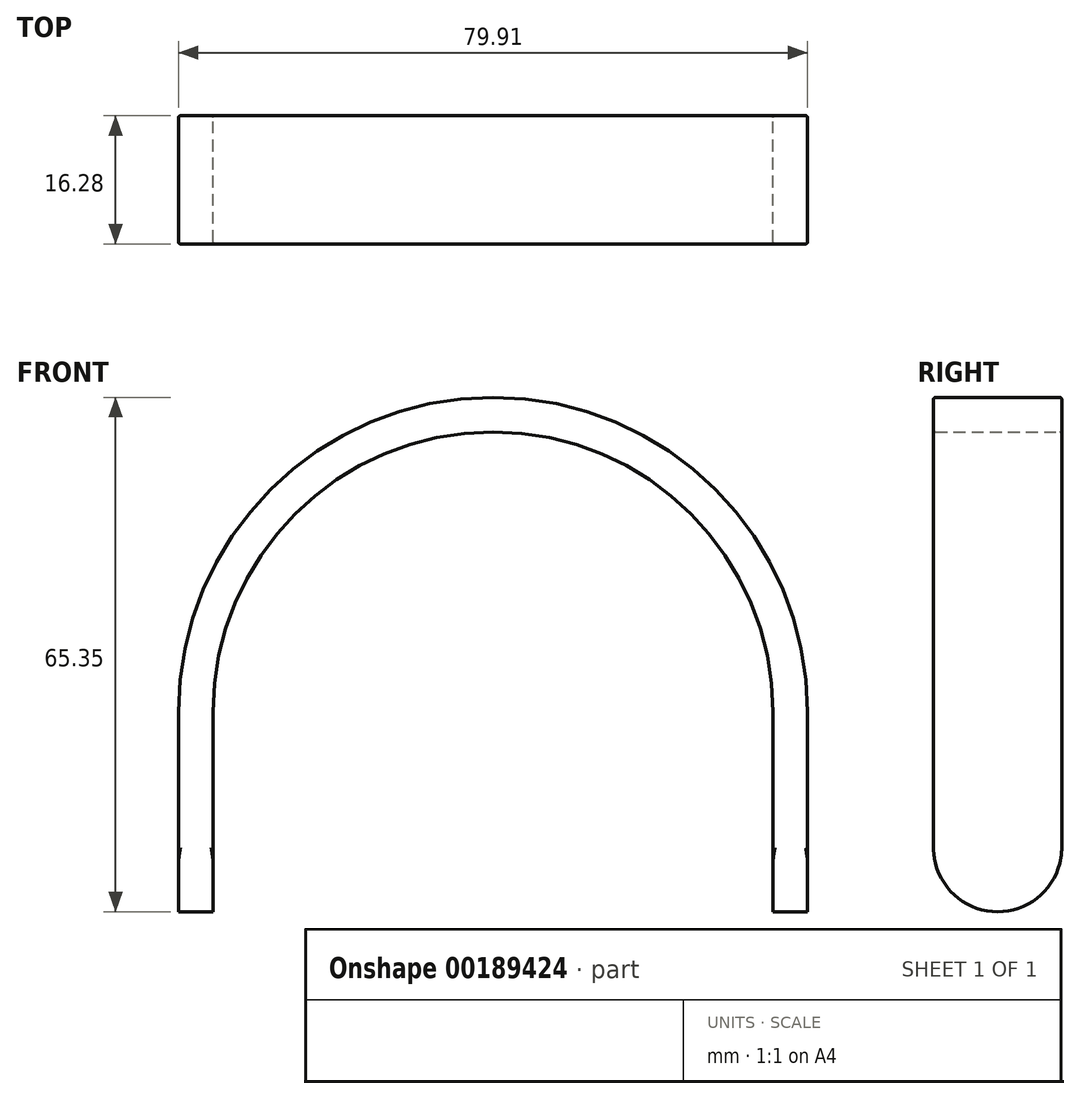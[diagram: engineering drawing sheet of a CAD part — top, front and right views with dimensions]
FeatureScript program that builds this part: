
annotation { "Feature Type Name" : "Feature", "Feature Type Description" : "" }
export const myFeature = defineFeature(function(context is Context, id is Id, definition is map)
    precondition{}
    {
        {
            var Q0;
            Q0=qCreatedBy(makeId("Front.planeOp"),FACE);
            var sketch = newSketch(context, id + "F0", { "sketchPlane" : qUnion([Q0])});
            skArc(sketch, "E0", {"start": v(79.9, 0) * mm, "mid": v(39.95, 39.95) * mm, "end": v(0, 0) * mm});
            skArc(sketch, "E1", {"start": v(75.51, 0) * mm, "mid": v(39.95, 35.56) * mm, "end": v(4.4, 0) * mm});
            skLineSegment(sketch, "E2", {"start": v(4.4, 0) * mm, "end": v(0, 0) * mm});
            skLineSegment(sketch, "E3", {"start": v(75.51, 0) * mm, "end": v(79.9, 0) * mm});
            skSolve(sketch);
        }
        {
            var Q0;
            Q0 = qSketchRegion(id + "F0", true);
            extrude(context, id + "F1", {"entities" : qUnion([Q0]), "depth" : 16.28 * mm});
        }
        {
            var Q0;
            Q0=makeQuery(id+"F1.opExtrude","CAP_EDGE",EDGE,{"disambiguationData":[OSD([sQuery(id+"F0.wireOp",EDGE,"E0")])],"isStart":false});
            var Q1;
            Q1=makeQuery(id+"F1.opExtrude","CAP_EDGE",EDGE,{"disambiguationData":[OSD([sQuery(id+"F0.wireOp",EDGE,"E1")])],"isStart":false});
            var Q2;
            Q2=makeQuery(id+"F1.opExtrude","CAP_EDGE",EDGE,{"disambiguationData":[OSD([sQuery(id+"F0.wireOp",EDGE,"E0")])],"isStart":true});
            var Q3;
            Q3=makeQuery(id+"F1.opExtrude","CAP_EDGE",EDGE,{"disambiguationData":[OSD([sQuery(id+"F0.wireOp",EDGE,"E1")])],"isStart":true});
            fillet(context, id + "F2", {"entities" : qUnion([Q0, Q1, Q2, Q3]), "radius" : 0.25 * mm, "tangentPropagation" : true, "allowEdgeOverflow" : false});
        }
        {
            var Q0;
            Q0=makeQuery(id+"F1.opExtrude","SWEPT_FACE",FACE,{"disambiguationData":[OSD([sQuery(id+"F0.wireOp",EDGE,"E2")])]});
            var sketch = newSketch(context, id + "F3", { "sketchPlane" : qUnion([Q0])});
            skLineSegment(sketch, "E4.0.0", {"start": v(0, 16.03) * mm, "end": v(0, 0.25) * mm});
            skArc(sketch, "E4.0.1", {"start": v(0, 0.25) * mm, "mid": v(0.07, 0.07) * mm, "end": v(0.25, 0) * mm});
            skLineSegment(sketch, "E4.0.2", {"start": v(0.25, 0) * mm, "end": v(4.14, 0) * mm});
            skArc(sketch, "E4.0.3", {"start": v(4.14, 0) * mm, "mid": v(4.32, 0.07) * mm, "end": v(4.4, 0.25) * mm});
            skLineSegment(sketch, "E4.0.4", {"start": v(4.4, 0.25) * mm, "end": v(4.4, 16.03) * mm});
            skArc(sketch, "E4.0.5", {"start": v(4.4, 16.03) * mm, "mid": v(4.32, 16.2) * mm, "end": v(4.14, 16.28) * mm});
            skLineSegment(sketch, "E4.0.6", {"start": v(4.14, 16.28) * mm, "end": v(0.25, 16.28) * mm});
            skArc(sketch, "E4.0.7", {"start": v(0.25, 16.28) * mm, "mid": v(0.07, 16.2) * mm, "end": v(0, 16.03) * mm});
            skLineSegment(sketch, "E5.0.0", {"start": v(75.77, 0) * mm, "end": v(79.65, 0) * mm});
            skArc(sketch, "E5.0.1", {"start": v(79.65, 0) * mm, "mid": v(79.83, 0.07) * mm, "end": v(79.9, 0.25) * mm});
            skLineSegment(sketch, "E5.0.2", {"start": v(79.9, 0.25) * mm, "end": v(79.9, 16.03) * mm});
            skArc(sketch, "E5.0.3", {"start": v(79.9, 16.03) * mm, "mid": v(79.83, 16.2) * mm, "end": v(79.65, 16.28) * mm});
            skLineSegment(sketch, "E5.0.4", {"start": v(79.65, 16.28) * mm, "end": v(75.77, 16.28) * mm});
            skArc(sketch, "E5.0.5", {"start": v(75.77, 16.28) * mm, "mid": v(75.59, 16.2) * mm, "end": v(75.51, 16.03) * mm});
            skLineSegment(sketch, "E5.0.6", {"start": v(75.51, 16.03) * mm, "end": v(75.51, 0.25) * mm});
            skArc(sketch, "E5.0.7", {"start": v(75.51, 0.25) * mm, "mid": v(75.59, 0.07) * mm, "end": v(75.77, 0) * mm});
            skSolve(sketch);
        }
        {
            var Q0;
            Q0 = qSketchRegion(id + "F3", true);
            extrude(context, id + "F4", {"entities" : qUnion([Q0]), "operationType" : NewBodyOperationType.ADD, "depth" : 25.4 * mm});
        }
        {
            var Q0;
            Q0=makeQuery(id+"F4.opExtrude","SWEPT_FACE",FACE,{"disambiguationData":[OSD([sQuery(id+"F3.wireOp",EDGE,"E4.0.0")])]});
            var sketch = newSketch(context, id + "F5", { "sketchPlane" : qUnion([Q0])});
            skArc(sketch, "E6", {"start": v(0, -17.26) * mm, "mid": v(8.14, -25.4) * mm, "end": v(16.28, -17.26) * mm});
            skLineSegment(sketch, "E7", {"start": v(16.28, -17.26) * mm, "end": v(0, -17.26) * mm, "construction": true});
            skLineSegment(sketch, "E8", {"start": v(16.28, -17.26) * mm, "end": v(16.28, -26.57) * mm});
            skLineSegment(sketch, "E9", {"start": v(16.28, -26.57) * mm, "end": v(0, -26.57) * mm});
            skLineSegment(sketch, "E10", {"start": v(0, -26.57) * mm, "end": v(0, -17.26) * mm});
            skSolve(sketch);
        }
        {
            var Q0;
            Q0 = qSketchRegion(id + "F5", true);
            extrude(context, id + "F6", {"entities" : qUnion([Q0]), "operationType" : NewBodyOperationType.REMOVE, "endBound" : BoundingType.THROUGH_ALL, "oppositeDirection" : true, "depth" : 25.4 * mm});
        }
    });
